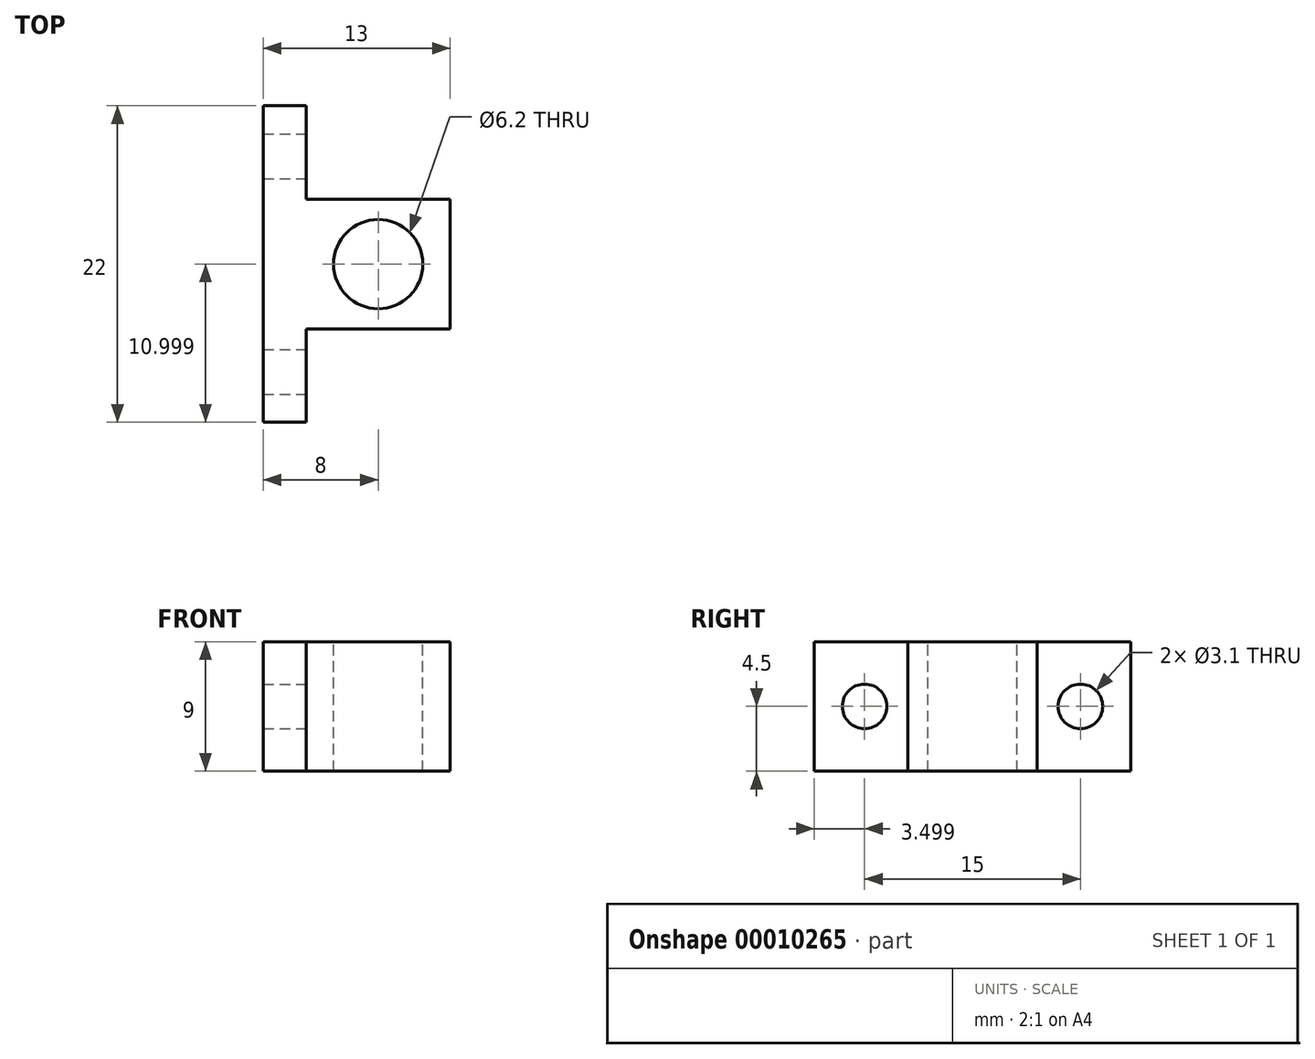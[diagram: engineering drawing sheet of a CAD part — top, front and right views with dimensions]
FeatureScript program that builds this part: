
annotation { "Feature Type Name" : "Feature", "Feature Type Description" : "" }
export const myFeature = defineFeature(function(context is Context, id is Id, definition is map)
    precondition{}
    {
        {
            var Q0;
            Q0=qCreatedBy(makeId("Top.planeOp"),FACE);
            var sketch = newSketch(context, id + "F0", { "sketchPlane" : qUnion([Q0])});
            skLineSegment(sketch, "E0.bottom", {"start": v(-10, -4.7) * mm, "end": v(-13, -4.7) * mm});
            skLineSegment(sketch, "E0.top", {"start": v(-10, 17.3) * mm, "end": v(-13, 17.3) * mm});
            skLineSegment(sketch, "E0.left", {"start": v(-10, -4.7) * mm, "end": v(-10, 1.8) * mm});
            skLineSegment(sketch, "E0.right", {"start": v(-13, -4.7) * mm, "end": v(-13, 17.3) * mm});
            skLineSegment(sketch, "E1.bottom", {"start": v(-10, 1.8) * mm, "end": v(0, 1.8) * mm});
            skLineSegment(sketch, "E1.top", {"start": v(-10, 10.8) * mm, "end": v(0, 10.8) * mm});
            skLineSegment(sketch, "E1.right", {"start": v(0, 1.8) * mm, "end": v(0, 10.8) * mm});
            skLineSegment(sketch, "E2.trimOffspring", {"start": v(-10, 10.8) * mm, "end": v(-10, 17.3) * mm});
            skSolve(sketch);
        }
        {
            var Q0;
            Q0=makeQuery(id+"F0.imprint","IMPRINT",FACE,{"disambiguationData":[TD([[makeQuery(id+"F0.imprint","IMPRINT",EDGE,{"derivedFrom":sQuery(id+"F0.wireOp",EDGE,"E0.bottom")}),-1.0]])]});
            extrude(context, id + "F1", {"entities" : qUnion([Q0]), "depth" : 9 * mm});
        }
        {
            var Q0;
            Q0=makeQuery(id+"F1.opExtrude","CAP_FACE",FACE,{"disambiguationData":[OSD([sQuery(id+"F0.wireOp",EDGE,"E0.bottom"),sQuery(id+"F0.wireOp",EDGE,"E0.top"),sQuery(id+"F0.wireOp",EDGE,"E0.left"),sQuery(id+"F0.wireOp",EDGE,"E0.right"),sQuery(id+"F0.wireOp",EDGE,"E1.bottom"),sQuery(id+"F0.wireOp",EDGE,"E1.top"),sQuery(id+"F0.wireOp",EDGE,"E1.right"),sQuery(id+"F0.wireOp",EDGE,"E2.trimOffspring")])],"isStart":false});
            var sketch = newSketch(context, id + "F2", { "sketchPlane" : qUnion([Q0])});
            skCircle(sketch, "E3", {"center": v(-5, 6.3) * mm, "radius": 3.1 * mm});
            skSolve(sketch);
        }
        {
            var Q0;
            Q0=makeQuery(id+"F2.imprint","IMPRINT",FACE,{"disambiguationData":[TD([[makeQuery(id+"F2.imprint","IMPRINT",EDGE,{"derivedFrom":sQuery(id+"F2.wireOp",EDGE,"E3")}),1.0]])]});
            extrude(context, id + "F3", {"entities" : qUnion([Q0]), "operationType" : NewBodyOperationType.REMOVE, "endBound" : BoundingType.THROUGH_ALL, "oppositeDirection" : true, "depth" : 25 * mm});
        }
        {
            var Q0;
            Q0=makeQuery(id+"F1.opExtrude","SWEPT_FACE",FACE,{"disambiguationData":[OSD([sQuery(id+"F0.wireOp",EDGE,"E0.left")])]});
            var sketch = newSketch(context, id + "F4", { "sketchPlane" : qUnion([Q0])});
            skCircle(sketch, "E4", {"center": v(-1.2, 4.5) * mm, "radius": 1.55 * mm});
            skSolve(sketch);
        }
        {
            var Q0;
            Q0=makeQuery(id+"F4.imprint","IMPRINT",FACE,{"disambiguationData":[TD([[makeQuery(id+"F4.imprint","IMPRINT",EDGE,{"derivedFrom":sQuery(id+"F4.wireOp",EDGE,"E4")}),1.0]])]});
            extrude(context, id + "F5", {"entities" : qUnion([Q0]), "operationType" : NewBodyOperationType.REMOVE, "endBound" : BoundingType.THROUGH_ALL, "oppositeDirection" : true, "depth" : 25 * mm});
        }
        {
            var Q0;
            Q0=makeQuery(id+"F1.opExtrude","SWEPT_FACE",FACE,{"disambiguationData":[OSD([sQuery(id+"F0.wireOp",EDGE,"E2.trimOffspring")])]});
            var sketch = newSketch(context, id + "F6", { "sketchPlane" : qUnion([Q0])});
            skCircle(sketch, "E5", {"center": v(13.8, 4.5) * mm, "radius": 1.55 * mm});
            skSolve(sketch);
        }
        {
            var Q0;
            Q0=makeQuery(id+"F6.imprint","IMPRINT",FACE,{"disambiguationData":[TD([[makeQuery(id+"F6.imprint","IMPRINT",EDGE,{"derivedFrom":sQuery(id+"F6.wireOp",EDGE,"E5")}),1.0]])]});
            extrude(context, id + "F7", {"entities" : qUnion([Q0]), "operationType" : NewBodyOperationType.REMOVE, "endBound" : BoundingType.THROUGH_ALL, "oppositeDirection" : true, "depth" : 25 * mm});
        }
    });
